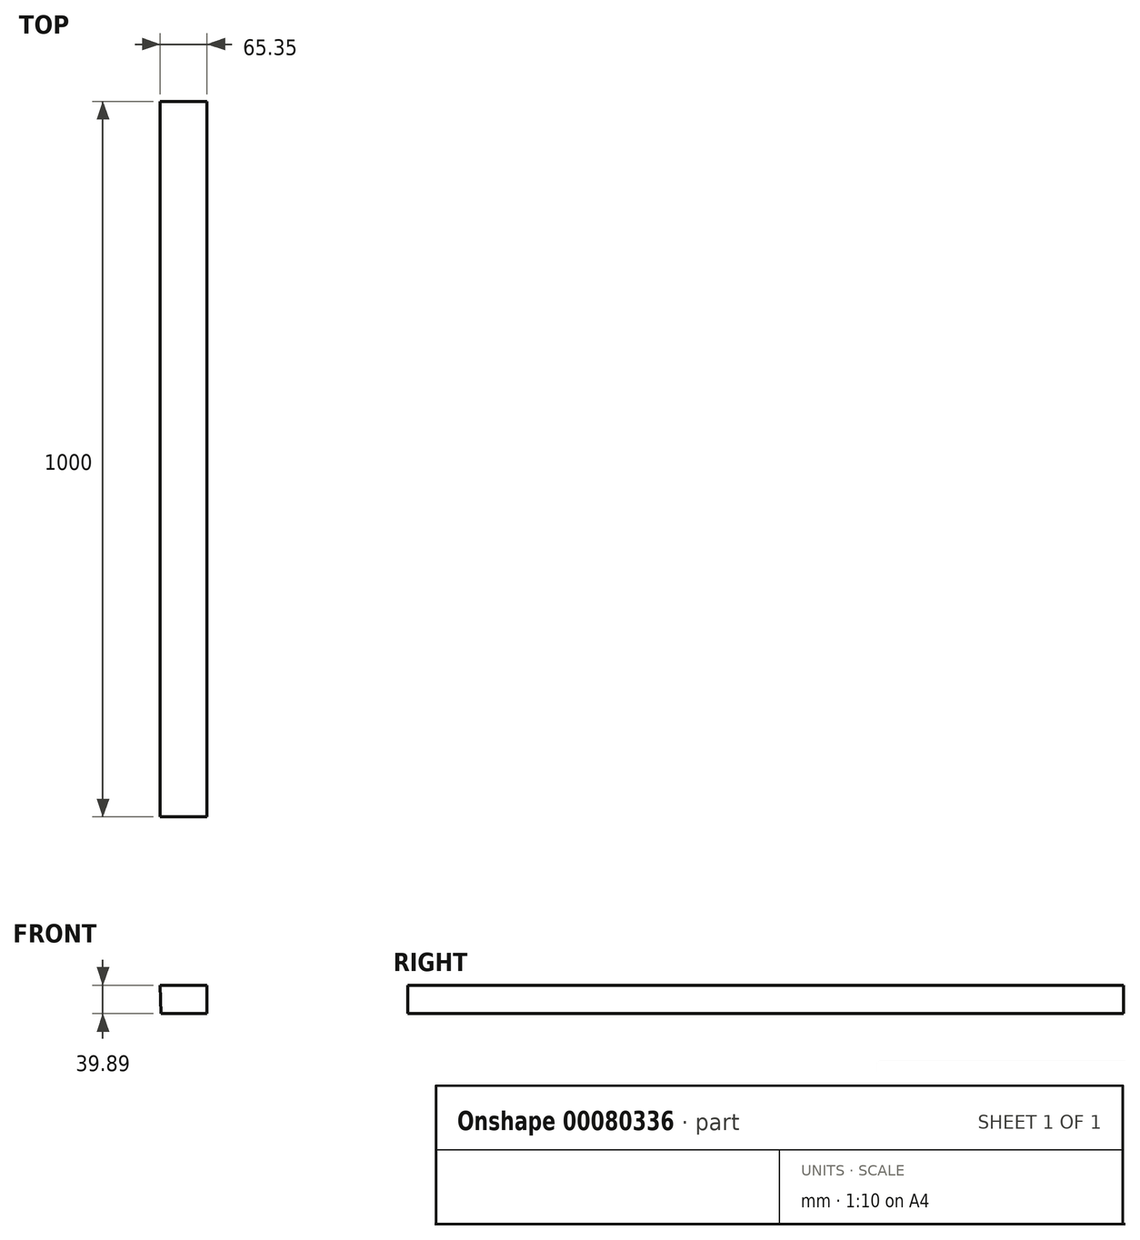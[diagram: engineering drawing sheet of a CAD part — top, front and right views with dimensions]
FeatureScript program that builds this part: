
annotation { "Feature Type Name" : "Feature", "Feature Type Description" : "" }
export const myFeature = defineFeature(function(context is Context, id is Id, definition is map)
    precondition{}
    {
        {
            var Q0;
            Q0=qCreatedBy(makeId("Front.planeOp"),FACE);
            var sketch = newSketch(context, id + "F0", { "sketchPlane" : qUnion([Q0])});
            skLineSegment(sketch, "E0", {"start": v(0, 0) * mm, "end": v(65.35, 0) * mm});
            skLineSegment(sketch, "E1", {"start": v(65.35, 0) * mm, "end": v(65.35, 39.89) * mm});
            skLineSegment(sketch, "E2", {"start": v(65.35, 39.89) * mm, "end": v(0, 39.89) * mm});
            skLineSegment(sketch, "E3", {"start": v(0, 39.89) * mm, "end": v(1.01, -3) * mm});
            skSolve(sketch);
        }
        {
            var Q0;
            Q0 = qSketchRegion(id + "F0", true);
            extrude(context, id + "F1", {"entities" : qUnion([Q0]), "depth" : 1000 * mm});
        }
    });
